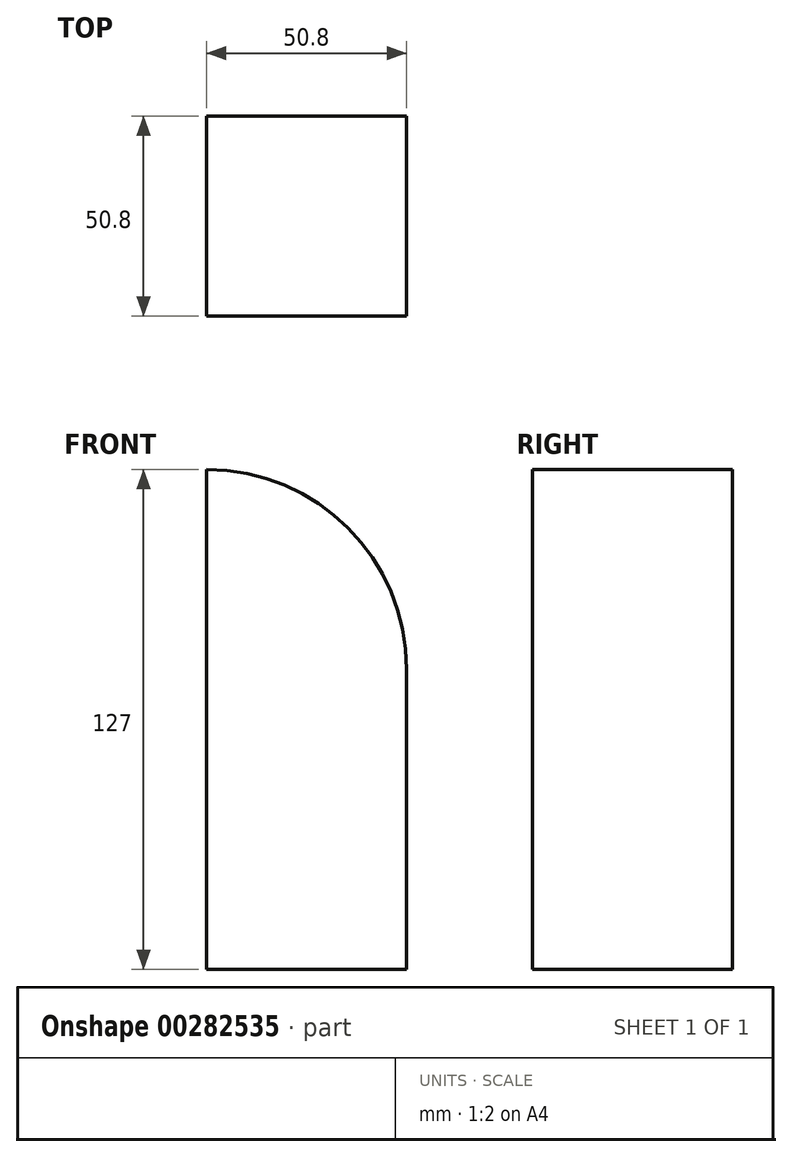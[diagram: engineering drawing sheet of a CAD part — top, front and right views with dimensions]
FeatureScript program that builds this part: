
annotation { "Feature Type Name" : "Feature", "Feature Type Description" : "" }
export const myFeature = defineFeature(function(context is Context, id is Id, definition is map)
    precondition{}
    {
        {
            var Q0;
            Q0=qCreatedBy(makeId("Top.planeOp"),FACE);
            var sketch = newSketch(context, id + "F0", { "sketchPlane" : qUnion([Q0])});
            skLineSegment(sketch, "E0.bottom", {"start": v(-25.4, 25.4) * mm, "end": v(25.4, 25.4) * mm});
            skLineSegment(sketch, "E0.top", {"start": v(-25.4, -25.4) * mm, "end": v(25.4, -25.4) * mm});
            skLineSegment(sketch, "E0.left", {"start": v(-25.4, 25.4) * mm, "end": v(-25.4, -25.4) * mm});
            skLineSegment(sketch, "E0.right", {"start": v(25.4, 25.4) * mm, "end": v(25.4, -25.4) * mm});
            skPoint(sketch, "E0.middle", {"position": v(0, 0) * mm});
            skSolve(sketch);
        }
        {
            var Q0;
            Q0 = qSketchRegion(id + "F0", true);
            extrude(context, id + "F1", {"entities" : qUnion([Q0]), "endBound" : BoundingType.SYMMETRIC, "depth" : 127 * mm});
        }
        {
            var Q0;
            Q0=makeQuery(id+"F1.opExtrude","CAP_EDGE",EDGE,{"disambiguationData":[OSD([sQuery(id+"F0.wireOp",EDGE,"E0.right")])],"isStart":false});
            fillet(context, id + "F2", {"entities" : qUnion([Q0]), "radius" : 50.8 * mm, "tangentPropagation" : true, "allowEdgeOverflow" : false});
        }
    });
